FCSTD DOCUMENT  (FreeCAD 0.21R33771 (Git))
Label: RING0
License: All rights reserved
LicenseURL: http://en.wikipedia.org/wiki/All_rights_reserved
objects: Part::Part2DObjectPython×168, App::FeaturePython×24, App::DocumentObjectGroup×2
note: 168 computed .brp shape members not serialized (recipe doc carries the construction recipe); baked Part::Feature solids carry a one-line shape summary decoded from their .brp

FEATURE [Part::Part2DObjectPython] Rectangle  # Draft 2D object (typed FeaturePython)
  Area = 0
  ChamferSize = 0
  Columns = 1
  FilletRadius = 0
  Height = 6
  Length = 6
  MakeFace = false
  Placement = pos=(275.649,-48.4904,0) rot=(0,0,1;1.77186rad)
  Rows = 1
FEATURE [App::FeaturePython] Text  # WARN: FeaturePython — macro-defined, semantics opaque (R4)
  Placement = pos=(270.79,-53.3517,0) rot=(0,0,-1;4.73892rad)
  Text = 0
FEATURE [App::FeaturePython] Text001  # WARN: FeaturePython — macro-defined, semantics opaque (R4)
  Placement = pos=(268.047,49.5386,0) rot=(0,0,1;2.6241rad)
  Text = 6.
FEATURE [Part::Part2DObjectPython] Circle  # Draft 2D object (typed FeaturePython)
  Area = 1.13097
  FirstAngle = 0
  LastAngle = 0
  MakeFace = true
  Placement = pos=(271.391,-42.6225,0) rot=(0,0,1;1.77186rad)
  Radius = 0.6
FEATURE [Part::Part2DObjectPython] Rectangle001  # Draft 2D object (typed FeaturePython)
  Area = 0
  ChamferSize = 0
  Columns = 1
  FilletRadius = 0
  Height = 6
  Length = 6
  MakeFace = false
  Placement = pos=(277.924,-33.0065,0) rot=(0,0,1;1.823rad)
  Rows = 1
FEATURE [Part::Part2DObjectPython] Circle001  # Draft 2D object (typed FeaturePython)
  Area = 1.13097
  FirstAngle = 0
  LastAngle = 0
  MakeFace = true
  Placement = pos=(273.372,-27.3639,0) rot=(0,0,1;1.823rad)
  Radius = 0.6
FEATURE [Part::Part2DObjectPython] Rectangle002  # Draft 2D object (typed FeaturePython)
  Area = 0
  ChamferSize = 0
  Columns = 1
  FilletRadius = 0
  Height = 6
  Length = 6
  MakeFace = false
  Placement = pos=(279.312,-17.449,0) rot=(0,0,1;1.86558rad)
  Rows = 1
FEATURE [Part::Part2DObjectPython] Circle002  # Draft 2D object (typed FeaturePython)
  Area = 1.13097
  FirstAngle = 0
  LastAngle = 0
  MakeFace = true
  Placement = pos=(274.524,-12.0053,0) rot=(0,0,1;1.86558rad)
  Radius = 0.6
FEATURE [Part::Part2DObjectPython] Rectangle003  # Draft 2D object (typed FeaturePython)
  Area = 0
  ChamferSize = 0
  Columns = 1
  FilletRadius = 0
  Height = 6
  Length = 6
  MakeFace = false
  Placement = pos=(279.797,-1.89239,0) rot=(0,0,1;1.89386rad)
  Rows = 1
FEATURE [Part::Part2DObjectPython] Circle003  # Draft 2D object (typed FeaturePython)
  Area = 1.13097
  FirstAngle = 0
  LastAngle = 0
  MakeFace = true
  Placement = pos=(274.857,3.41377,0) rot=(0,0,1;1.89386rad)
  Radius = 0.6
FEATURE [Part::Part2DObjectPython] Rectangle004  # Draft 2D object (typed FeaturePython)
  Area = 0
  ChamferSize = 0
  Columns = 1
  FilletRadius = 0
  Height = 6
  Length = 6
  MakeFace = false
  Placement = pos=(279.385,13.5935,0) rot=(0,0,1;1.90328rad)
  Rows = 1
FEATURE [Part::Part2DObjectPython] Circle004  # Draft 2D object (typed FeaturePython)
  Area = 1.13097
  FirstAngle = 0
  LastAngle = 0
  MakeFace = true
  Placement = pos=(274.395,18.8528,0) rot=(0,0,1;1.90328rad)
  Radius = 0.6
FEATURE [Part::Part2DObjectPython] Rectangle005  # Draft 2D object (typed FeaturePython)
  Area = 0
  ChamferSize = 0
  Columns = 1
  FilletRadius = 0
  Height = 6
  Length = 6
  MakeFace = false
  Placement = pos=(278.071,28.9642,0) rot=(0,0,1;1.8956rad)
  Rows = 1
FEATURE [Part::Part2DObjectPython] Circle005  # Draft 2D object (typed FeaturePython)
  Area = 1.13097
  FirstAngle = 0
  LastAngle = 0
  MakeFace = true
  Placement = pos=(273.121,34.2618,0) rot=(0,0,1;1.8956rad)
  Radius = 0.6
FEATURE [Part::Part2DObjectPython] Rectangle006  # Draft 2D object (typed FeaturePython)
  Area = 0
  ChamferSize = 0
  Columns = 1
  FilletRadius = 0
  Height = 6
  Length = 6
  MakeFace = false
  Placement = pos=(275.882,44.2081,0) rot=(0,0,1;1.88077rad)
  Rows = 1
FEATURE [Part::Part2DObjectPython] Circle006  # Draft 2D object (typed FeaturePython)
  Area = 1.13097
  FirstAngle = 0
  LastAngle = 0
  MakeFace = true
  Placement = pos=(271.012,49.5784,0) rot=(0,0,1;1.88077rad)
  Radius = 0.6
FEATURE [Part::Part2DObjectPython] Rectangle007  # Draft 2D object (typed FeaturePython)
  Area = 0
  ChamferSize = 0
  Columns = 1
  FilletRadius = 0
  Height = 6
  Length = 6
  MakeFace = false
  Placement = pos=(262.844,95.0543,0) rot=(0,0,1;2.10958rad)
  Rows = 1
FEATURE [App::FeaturePython] Text002  # WARN: FeaturePython — macro-defined, semantics opaque (R4)
  Placement = pos=(261.188,89.1931,0) rot=(0,0,-1;4.21532rad)
  Text = 0
FEATURE [App::FeaturePython] Text003  # WARN: FeaturePython — macro-defined, semantics opaque (R4)
  Placement = pos=(207.363,176.926,0) rot=(0,0,1;3.1477rad)
  Text = 7
FEATURE [Part::Part2DObjectPython] Circle007  # Draft 2D object (typed FeaturePython)
  Area = 1.13097
  FirstAngle = 0
  LastAngle = 0
  MakeFace = true
  Placement = pos=(256.883,99.18,0) rot=(0,0,1;2.10958rad)
  Radius = 0.6
FEATURE [Part::Part2DObjectPython] Rectangle008  # Draft 2D object (typed FeaturePython)
  Area = 0
  ChamferSize = 0
  Columns = 1
  FilletRadius = 0
  Height = 6
  Length = 6
  MakeFace = false
  Placement = pos=(257.154,110.988,0) rot=(0,0,1;2.49058rad)
  Rows = 1
FEATURE [Part::Part2DObjectPython] Circle008  # Draft 2D object (typed FeaturePython)
  Area = 1.13097
  FirstAngle = 0
  LastAngle = 0
  MakeFace = true
  Placement = pos=(250.086,112.602,0) rot=(0,0,1;2.49058rad)
  Radius = 0.6
FEATURE [Part::Part2DObjectPython] Rectangle009  # Draft 2D object (typed FeaturePython)
  Area = 0
  ChamferSize = 0
  Columns = 1
  FilletRadius = 0
  Height = 6
  Length = 6
  MakeFace = false
  Placement = pos=(247.728,128.429,0) rot=(0,0,1;3.60114rad)
  Rows = 1
FEATURE [Part::Part2DObjectPython] Circle009  # Draft 2D object (typed FeaturePython)
  Area = 1.13097
  FirstAngle = 0
  LastAngle = 0
  MakeFace = true
  Placement = pos=(243.143,122.813,0) rot=(0,0,1;3.60114rad)
  Radius = 0.6
FEATURE [Part::Part2DObjectPython] Rectangle010  # Draft 2D object (typed FeaturePython)
  Area = 0
  ChamferSize = 0
  Columns = 1
  FilletRadius = 0
  Height = 6
  Length = 6
  MakeFace = false
  Placement = pos=(236.735,141.575,0) rot=(0,0,1;4.49579rad)
  Rows = 1
FEATURE [Part::Part2DObjectPython] Circle010  # Draft 2D object (typed FeaturePython)
  Area = 1.13097
  FirstAngle = 0
  LastAngle = 0
  MakeFace = true
  Placement = pos=(238.246,134.484,0) rot=(0,0,1;4.49579rad)
  Radius = 0.6
FEATURE [Part::Part2DObjectPython] Rectangle011  # Draft 2D object (typed FeaturePython)
  Area = 0
  ChamferSize = 0
  Columns = 1
  FilletRadius = 0
  Height = 6
  Length = 6
  MakeFace = false
  Placement = pos=(227.423,153.562,0) rot=(0,0,1;4.896rad)
  Rows = 1
FEATURE [Part::Part2DObjectPython] Circle011  # Draft 2D object (typed FeaturePython)
  Area = 1.13097
  FirstAngle = 0
  LastAngle = 0
  MakeFace = true
  Placement = pos=(231.577,147.621,0) rot=(0,0,1;4.896rad)
  Radius = 0.6
FEATURE [Part::Part2DObjectPython] Rectangle012  # Draft 2D object (typed FeaturePython)
  Area = 0
  ChamferSize = 0
  Columns = 1
  FilletRadius = 0
  Height = 6
  Length = 6
  MakeFace = false
  Placement = pos=(218.11,165.292,0) rot=(0,0,1;5.15099rad)
  Rows = 1
FEATURE [Part::Part2DObjectPython] Circle012  # Draft 2D object (typed FeaturePython)
  Area = 1.13097
  FirstAngle = 0
  LastAngle = 0
  MakeFace = true
  Placement = pos=(223.629,160.591,0) rot=(0,0,1;5.15099rad)
  Radius = 0.6
FEATURE [Part::Part2DObjectPython] Rectangle013  # Draft 2D object (typed FeaturePython)
  Area = 0
  ChamferSize = 0
  Columns = 1
  FilletRadius = 0
  Height = 6
  Length = 6
  MakeFace = false
  Placement = pos=(208.376,176.591,0) rot=(0,0,1;5.36287rad)
  Rows = 1
FEATURE [Part::Part2DObjectPython] Circle013  # Draft 2D object (typed FeaturePython)
  Area = 1.13097
  FirstAngle = 0
  LastAngle = 0
  MakeFace = true
  Placement = pos=(214.76,173.155,0) rot=(0,0,1;5.36287rad)
  Radius = 0.6
FEATURE [Part::Part2DObjectPython] Rectangle014  # Draft 2D object (typed FeaturePython)
  Area = 0
  ChamferSize = 0
  Columns = 1
  FilletRadius = 0
  Height = 6
  Length = 6
  MakeFace = false
  Placement = pos=(172.246,210.641,0) rot=(0,0,1;5.97234rad)
  Rows = 1
FEATURE [App::FeaturePython] Text004  # WARN: FeaturePython — macro-defined, semantics opaque (R4)
  Placement = pos=(181.597,207.836,0) rot=(0,0,-1;3.69172rad)
  Text = 0
FEATURE [App::FeaturePython] Text005  # WARN: FeaturePython — macro-defined, semantics opaque (R4)
  Placement = pos=(91.1209,256.902,0) rot=(0,0,1;3.6713rad)
  Text = 8
FEATURE [Part::Part2DObjectPython] Circle014  # Draft 2D object (typed FeaturePython)
  Area = 1.13097
  FirstAngle = 0
  LastAngle = 0
  MakeFace = true
  Placement = pos=(179.447,211.479,0) rot=(0,0,1;5.97234rad)
  Radius = 0.6
FEATURE [Part::Part2DObjectPython] Rectangle015  # Draft 2D object (typed FeaturePython)
  Area = 0
  ChamferSize = 0
  Columns = 1
  FilletRadius = 0
  Height = 6
  Length = 6
  MakeFace = false
  Placement = pos=(160.438,219.579,0) rot=(0,0,1;6.13413rad)
  Rows = 1
FEATURE [Part::Part2DObjectPython] Circle015  # Draft 2D object (typed FeaturePython)
  Area = 1.13097
  FirstAngle = 0
  LastAngle = 0
  MakeFace = true
  Placement = pos=(167.41,221.565,0) rot=(0,0,1;6.13413rad)
  Radius = 0.6
FEATURE [Part::Part2DObjectPython] Rectangle016  # Draft 2D object (typed FeaturePython)
  Area = 0
  ChamferSize = 0
  Columns = 1
  FilletRadius = 0
  Height = 6
  Length = 6
  MakeFace = false
  Placement = pos=(148.157,227.923,0) rot=(0,0,1;6.28214rad)
  Rows = 1
FEATURE [Part::Part2DObjectPython] Circle016  # Draft 2D object (typed FeaturePython)
  Area = 1.13097
  FirstAngle = 0
  LastAngle = 0
  MakeFace = true
  Placement = pos=(154.76,230.916,0) rot=(0,0,1;6.28214rad)
  Radius = 0.6
FEATURE [Part::Part2DObjectPython] Rectangle017  # Draft 2D object (typed FeaturePython)
  Area = 0
  ChamferSize = 0
  Columns = 1
  FilletRadius = 0
  Height = 6
  Length = 6
  MakeFace = false
  Placement = pos=(135.397,235.67,0) rot=(0,0,1;0.124791rad)
  Rows = 1
FEATURE [Part::Part2DObjectPython] Circle017  # Draft 2D object (typed FeaturePython)
  Area = 1.13097
  FirstAngle = 0
  LastAngle = 0
  MakeFace = true
  Placement = pos=(141.572,239.468,0) rot=(0,0,1;0.124791rad)
  Radius = 0.6
FEATURE [Part::Part2DObjectPython] Rectangle018  # Draft 2D object (typed FeaturePython)
  Area = 0
  ChamferSize = 0
  Columns = 1
  FilletRadius = 0
  Height = 6
  Length = 6
  MakeFace = false
  Placement = pos=(122.129,242.793,0) rot=(0,0,1;0.217817rad)
  Rows = 1
FEATURE [Part::Part2DObjectPython] Circle018  # Draft 2D object (typed FeaturePython)
  Area = 1.13097
  FirstAngle = 0
  LastAngle = 0
  MakeFace = true
  Placement = pos=(127.925,247.148,0) rot=(0,0,1;0.217817rad)
  Radius = 0.6
FEATURE [Part::Part2DObjectPython] Rectangle019  # Draft 2D object (typed FeaturePython)
  Area = 0
  ChamferSize = 0
  Columns = 1
  FilletRadius = 0
  Height = 6
  Length = 6
  MakeFace = false
  Placement = pos=(108.265,249.296,0) rot=(0,0,1;0.252549rad)
  Rows = 1
FEATURE [Part::Part2DObjectPython] Circle019  # Draft 2D object (typed FeaturePython)
  Area = 1.13097
  FirstAngle = 0
  LastAngle = 0
  MakeFace = true
  Placement = pos=(113.906,253.85,0) rot=(0,0,1;0.252549rad)
  Radius = 0.6
FEATURE [Part::Part2DObjectPython] Rectangle020  # Draft 2D object (typed FeaturePython)
  Area = 0
  ChamferSize = 0
  Columns = 1
  FilletRadius = 0
  Height = 6
  Length = 6
  MakeFace = false
  Placement = pos=(93.6729,255.243,0) rot=(0,0,1;0.179245rad)
  Rows = 1
FEATURE [Part::Part2DObjectPython] Circle020  # Draft 2D object (typed FeaturePython)
  Area = 1.13097
  FirstAngle = 0
  LastAngle = 0
  MakeFace = true
  Placement = pos=(99.6323,259.372,0) rot=(0,0,1;0.179245rad)
  Radius = 0.6
FEATURE [Part::Part2DObjectPython] Rectangle021  # Draft 2D object (typed FeaturePython)
  Area = 0
  ChamferSize = 0
  Columns = 1
  FilletRadius = 0
  Height = 6
  Length = 6
  MakeFace = false
  Placement = pos=(42.0451,271.038,0) rot=(0,0,1;5.7533rad)
  Rows = 1
FEATURE [App::FeaturePython] Text006  # WARN: FeaturePython — macro-defined, semantics opaque (R4)
  Placement = pos=(53.3517,270.79,0) rot=(0,0,-1;3.16812rad)
  Text = 0
FEATURE [App::FeaturePython] Text007  # WARN: FeaturePython — macro-defined, semantics opaque (R4)
  Placement = pos=(-49.5386,268.047,0) rot=(0,0,1;4.1949rad)
  Text = 9
FEATURE [Part::Part2DObjectPython] Circle021  # Draft 2D object (typed FeaturePython)
  Area = 1.13097
  FirstAngle = 0
  LastAngle = 0
  MakeFace = true
  Placement = pos=(49.2563,270.29,0) rot=(0,0,1;5.7533rad)
  Radius = 0.6
FEATURE [Part::Part2DObjectPython] Rectangle022  # Draft 2D object (typed FeaturePython)
  Area = 0
  ChamferSize = 0
  Columns = 1
  FilletRadius = 0
  Height = 6
  Length = 6
  MakeFace = false
  Placement = pos=(27.2061,272.097,0) rot=(0,0,1;6.03552rad)
  Rows = 1
FEATURE [Part::Part2DObjectPython] Circle022  # Draft 2D object (typed FeaturePython)
  Area = 1.13097
  FirstAngle = 0
  LastAngle = 0
  MakeFace = true
  Placement = pos=(34.3402,273.388,0) rot=(0,0,1;6.03552rad)
  Radius = 0.6
FEATURE [Part::Part2DObjectPython] Rectangle023  # Draft 2D object (typed FeaturePython)
  Area = 0
  ChamferSize = 0
  Columns = 1
  FilletRadius = 0
  Height = 6
  Length = 6
  MakeFace = false
  Placement = pos=(17.0338,271.634,0) rot=(0,0,1;1.16797rad)
  Rows = 1
FEATURE [Part::Part2DObjectPython] Circle023  # Draft 2D object (typed FeaturePython)
  Area = 1.13097
  FirstAngle = 0
  LastAngle = 0
  MakeFace = true
  Placement = pos=(16.8613,278.882,0) rot=(0,0,1;1.16797rad)
  Radius = 0.6
FEATURE [Part::Part2DObjectPython] Rectangle024  # Draft 2D object (typed FeaturePython)
  Area = 0
  ChamferSize = 0
  Columns = 1
  FilletRadius = 0
  Height = 6
  Length = 6
  MakeFace = false
  Placement = pos=(3.71464,273.95,0) rot=(0,0,1;1.85197rad)
  Rows = 1
FEATURE [Part::Part2DObjectPython] Circle024  # Draft 2D object (typed FeaturePython)
  Area = 1.13097
  FirstAngle = 0
  LastAngle = 0
  MakeFace = true
  Placement = pos=(-0.998936,279.459,0) rot=(0,0,1;1.85197rad)
  Radius = 0.6
FEATURE [Part::Part2DObjectPython] Rectangle025  # Draft 2D object (typed FeaturePython)
  Area = 0
  ChamferSize = 0
  Columns = 1
  FilletRadius = 0
  Height = 6
  Length = 6
  MakeFace = false
  Placement = pos=(-11.3587,274.447,0) rot=(0,0,1;2.08829rad)
  Rows = 1
FEATURE [Part::Part2DObjectPython] Circle025  # Draft 2D object (typed FeaturePython)
  Area = 1.13097
  FirstAngle = 0
  LastAngle = 0
  MakeFace = true
  Placement = pos=(-17.2309,278.699,0) rot=(0,0,1;2.08829rad)
  Radius = 0.6
FEATURE [Part::Part2DObjectPython] Rectangle026  # Draft 2D object (typed FeaturePython)
  Area = 0
  ChamferSize = 0
  Columns = 1
  FilletRadius = 0
  Height = 6
  Length = 6
  MakeFace = false
  Placement = pos=(-26.6422,273.727,0) rot=(0,0,1;2.22791rad)
  Rows = 1
FEATURE [Part::Part2DObjectPython] Circle026  # Draft 2D object (typed FeaturePython)
  Area = 1.13097
  FirstAngle = 0
  LastAngle = 0
  MakeFace = true
  Placement = pos=(-33.049,277.12,0) rot=(0,0,1;2.22791rad)
  Radius = 0.6
FEATURE [Part::Part2DObjectPython] Rectangle027  # Draft 2D object (typed FeaturePython)
  Area = 0
  ChamferSize = 0
  Columns = 1
  FilletRadius = 0
  Height = 6
  Length = 6
  MakeFace = false
  Placement = pos=(-41.9084,272.015,0) rot=(0,0,1;2.33385rad)
  Rows = 1
FEATURE [Part::Part2DObjectPython] Circle027  # Draft 2D object (typed FeaturePython)
  Area = 1.13097
  FirstAngle = 0
  LastAngle = 0
  MakeFace = true
  Placement = pos=(-48.6381,274.712,0) rot=(0,0,1;2.33385rad)
  Radius = 0.6
FEATURE [Part::Part2DObjectPython] Rectangle028  # Draft 2D object (typed FeaturePython)
  Area = 0
  ChamferSize = 0
  Columns = 1
  FilletRadius = 0
  Height = 6
  Length = 6
  MakeFace = false
  Placement = pos=(-92.004,259.872,0) rot=(0,0,1;2.62881rad)
  Rows = 1
FEATURE [App::FeaturePython] Text008  # WARN: FeaturePython — macro-defined, semantics opaque (R4)
  Placement = pos=(-89.1931,261.188,0) rot=(0,0,-1;2.64452rad)
  Text = 0
FEATURE [App::FeaturePython] Text009  # WARN: FeaturePython — macro-defined, semantics opaque (R4)
  Placement = pos=(-176.926,207.363,0) rot=(0,0,1;4.7185rad)
  Text = 10
FEATURE [Part::Part2DObjectPython] Circle028  # Draft 2D object (typed FeaturePython)
  Area = 1.13097
  FirstAngle = 0
  LastAngle = 0
  MakeFace = true
  Placement = pos=(-99.227,260.496,0) rot=(0,0,1;2.62881rad)
  Radius = 0.6
FEATURE [Part::Part2DObjectPython] Rectangle029  # Draft 2D object (typed FeaturePython)
  Area = 0
  ChamferSize = 0
  Columns = 1
  FilletRadius = 0
  Height = 6
  Length = 6
  MakeFace = false
  Placement = pos=(-106.463,254.481,0) rot=(0,0,1;2.72551rad)
  Rows = 1
FEATURE [Part::Part2DObjectPython] Circle029  # Draft 2D object (typed FeaturePython)
  Area = 1.13097
  FirstAngle = 0
  LastAngle = 0
  MakeFace = true
  Placement = pos=(-113.713,254.405,0) rot=(0,0,1;2.72551rad)
  Radius = 0.6
FEATURE [Part::Part2DObjectPython] Rectangle030  # Draft 2D object (typed FeaturePython)
  Area = 0
  ChamferSize = 0
  Columns = 1
  FilletRadius = 0
  Height = 6
  Length = 6
  MakeFace = false
  Placement = pos=(-120.643,248.321,0) rot=(0,0,1;2.83407rad)
  Rows = 1
FEATURE [Part::Part2DObjectPython] Circle030  # Draft 2D object (typed FeaturePython)
  Area = 1.13097
  FirstAngle = 0
  LastAngle = 0
  MakeFace = true
  Placement = pos=(-127.841,247.46,0) rot=(0,0,1;2.83407rad)
  Radius = 0.6
FEATURE [Part::Part2DObjectPython] Rectangle031  # Draft 2D object (typed FeaturePython)
  Area = 0
  ChamferSize = 0
  Columns = 1
  FilletRadius = 0
  Height = 6
  Length = 6
  MakeFace = false
  Placement = pos=(-135.001,242.021,0) rot=(0,0,1;3.14194rad)
  Rows = 1
FEATURE [Part::Part2DObjectPython] Circle031  # Draft 2D object (typed FeaturePython)
  Area = 1.13097
  FirstAngle = 0
  LastAngle = 0
  MakeFace = true
  Placement = pos=(-141.6,239.019,0) rot=(0,0,1;3.14194rad)
  Radius = 0.6
FEATURE [Part::Part2DObjectPython] Rectangle032  # Draft 2D object (typed FeaturePython)
  Area = 0
  ChamferSize = 0
  Columns = 1
  FilletRadius = 0
  Height = 6
  Length = 6
  MakeFace = false
  Placement = pos=(-148.162,233.922,0) rot=(0,0,1;3.14229rad)
  Rows = 1
FEATURE [Part::Part2DObjectPython] Circle032  # Draft 2D object (typed FeaturePython)
  Area = 1.13097
  FirstAngle = 0
  LastAngle = 0
  MakeFace = true
  Placement = pos=(-154.76,230.917,0) rot=(0,0,1;3.14229rad)
  Radius = 0.6
FEATURE [Part::Part2DObjectPython] Rectangle033  # Draft 2D object (typed FeaturePython)
  Area = 0
  ChamferSize = 0
  Columns = 1
  FilletRadius = 0
  Height = 6
  Length = 6
  MakeFace = false
  Placement = pos=(-161.278,225.474,0) rot=(0,0,1;3.27563rad)
  Rows = 1
FEATURE [Part::Part2DObjectPython] Circle033  # Draft 2D object (typed FeaturePython)
  Area = 1.13097
  FirstAngle = 0
  LastAngle = 0
  MakeFace = true
  Placement = pos=(-167.418,221.619,0) rot=(0,0,1;3.27563rad)
  Radius = 0.6
FEATURE [Part::Part2DObjectPython] Rectangle034  # Draft 2D object (typed FeaturePython)
  Area = 0
  ChamferSize = 0
  Columns = 1
  FilletRadius = 0
  Height = 6
  Length = 6
  MakeFace = false
  Placement = pos=(-174.05,216.338,0) rot=(0,0,1;3.44423rad)
  Rows = 1
FEATURE [Part::Part2DObjectPython] Circle034  # Draft 2D object (typed FeaturePython)
  Area = 1.13097
  FirstAngle = 0
  LastAngle = 0
  MakeFace = true
  Placement = pos=(-179.456,211.507,0) rot=(0,0,1;3.44423rad)
  Radius = 0.6
FEATURE [Part::Part2DObjectPython] Rectangle035  # Draft 2D object (typed FeaturePython)
  Area = 0
  ChamferSize = 0
  Columns = 1
  FilletRadius = 0
  Height = 6
  Length = 6
  MakeFace = false
  Placement = pos=(-213.973,180.027,0) rot=(0,0,1;4.26157rad)
  Rows = 1
FEATURE [App::FeaturePython] Text010  # WARN: FeaturePython — macro-defined, semantics opaque (R4)
  Placement = pos=(-207.836,181.597,0) rot=(0,0,-1;2.12092rad)
  Text = 0
FEATURE [App::FeaturePython] Text011  # WARN: FeaturePython — macro-defined, semantics opaque (R4)
  Placement = pos=(-256.902,91.1209,0) rot=(0,0,1;5.2421rad)
  Text = 11
FEATURE [Part::Part2DObjectPython] Circle035  # Draft 2D object (typed FeaturePython)
  Area = 1.13097
  FirstAngle = 0
  LastAngle = 0
  MakeFace = true
  Placement = pos=(-214.149,172.78,0) rot=(0,0,1;4.26157rad)
  Radius = 0.6
FEATURE [Part::Part2DObjectPython] Rectangle036  # Draft 2D object (typed FeaturePython)
  Area = 0
  ChamferSize = 0
  Columns = 1
  FilletRadius = 0
  Height = 6
  Length = 6
  MakeFace = false
  Placement = pos=(-224.768,167.149,0) rot=(0,0,1;4.60715rad)
  Rows = 1
FEATURE [Part::Part2DObjectPython] Circle036  # Draft 2D object (typed FeaturePython)
  Area = 1.13097
  FirstAngle = 0
  LastAngle = 0
  MakeFace = true
  Placement = pos=(-222.478,160.27,0) rot=(0,0,1;4.60715rad)
  Radius = 0.6
FEATURE [Part::Part2DObjectPython] Rectangle037  # Draft 2D object (typed FeaturePython)
  Area = 0
  ChamferSize = 0
  Columns = 1
  FilletRadius = 0
  Height = 6
  Length = 6
  MakeFace = false
  Placement = pos=(-234.676,153.133,0) rot=(0,0,1;5.01416rad)
  Rows = 1
FEATURE [Part::Part2DObjectPython] Circle037  # Draft 2D object (typed FeaturePython)
  Area = 1.13097
  FirstAngle = 0
  LastAngle = 0
  MakeFace = true
  Placement = pos=(-229.85,147.723,0) rot=(0,0,1;5.01416rad)
  Radius = 0.6
FEATURE [Part::Part2DObjectPython] Rectangle038  # Draft 2D object (typed FeaturePython)
  Area = 0
  ChamferSize = 0
  Columns = 1
  FilletRadius = 0
  Height = 6
  Length = 6
  MakeFace = false
  Placement = pos=(-243.261,138.127,0) rot=(0,0,1;5.46794rad)
  Rows = 1
FEATURE [Part::Part2DObjectPython] Circle038  # Draft 2D object (typed FeaturePython)
  Area = 1.13097
  FirstAngle = 0
  LastAngle = 0
  MakeFace = true
  Placement = pos=(-236.552,135.38,0) rot=(0,0,1;5.46794rad)
  Radius = 0.6
FEATURE [Part::Part2DObjectPython] Rectangle039  # Draft 2D object (typed FeaturePython)
  Area = 0
  ChamferSize = 0
  Columns = 1
  FilletRadius = 0
  Height = 6
  Length = 6
  MakeFace = false
  Placement = pos=(-250.243,122.679,0) rot=(0,0,1;5.91806rad)
  Rows = 1
FEATURE [Part::Part2DObjectPython] Circle039  # Draft 2D object (typed FeaturePython)
  Area = 1.13097
  FirstAngle = 0
  LastAngle = 0
  MakeFace = true
  Placement = pos=(-243.007,123.125,0) rot=(0,0,1;5.91806rad)
  Radius = 0.6
FEATURE [Part::Part2DObjectPython] Rectangle040  # Draft 2D object (typed FeaturePython)
  Area = 0
  ChamferSize = 0
  Columns = 1
  FilletRadius = 0
  Height = 6
  Length = 6
  MakeFace = false
  Placement = pos=(-255.827,107.302,0) rot=(0,0,1;0.040317rad)
  Rows = 1
FEATURE [Part::Part2DObjectPython] Circle040  # Draft 2D object (typed FeaturePython)
  Area = 1.13097
  FirstAngle = 0
  LastAngle = 0
  MakeFace = true
  Placement = pos=(-249.353,110.565,0) rot=(0,0,1;0.040317rad)
  Radius = 0.6
FEATURE [Part::Part2DObjectPython] Rectangle041  # Draft 2D object (typed FeaturePython)
  Area = 0
  ChamferSize = 0
  Columns = 1
  FilletRadius = 0
  Height = 6
  Length = 6
  MakeFace = false
  Placement = pos=(-260.388,92.1849,0) rot=(0,0,1;0.383798rad)
  Rows = 1
FEATURE [Part::Part2DObjectPython] Circle041  # Draft 2D object (typed FeaturePython)
  Area = 1.13097
  FirstAngle = 0
  LastAngle = 0
  MakeFace = true
  Placement = pos=(-255.392,97.438,0) rot=(0,0,1;0.383798rad)
  Radius = 0.6
FEATURE [Part::Part2DObjectPython] Rectangle042  # Draft 2D object (typed FeaturePython)
  Area = 0
  ChamferSize = 0
  Columns = 1
  FilletRadius = 0
  Height = 6
  Length = 6
  MakeFace = false
  Placement = pos=(-270.401,42.267,0) rot=(0,0,1;1.20009rad)
  Rows = 1
FEATURE [App::FeaturePython] Text012  # WARN: FeaturePython — macro-defined, semantics opaque (R4)
  Placement = pos=(-270.79,53.3517,0) rot=(0,0,-1;1.59733rad)
  Text = 0
FEATURE [App::FeaturePython] Text013  # WARN: FeaturePython — macro-defined, semantics opaque (R4)
  Placement = pos=(-268.047,-49.5386,0) rot=(0,0,1;5.7657rad)
  Text = 12
FEATURE [Part::Part2DObjectPython] Circle042  # Draft 2D object (typed FeaturePython)
  Area = 1.13097
  FirstAngle = 0
  LastAngle = 0
  MakeFace = true
  Placement = pos=(-270.806,49.5055,0) rot=(0,0,1;1.20009rad)
  Radius = 0.6
FEATURE [Part::Part2DObjectPython] Rectangle043  # Draft 2D object (typed FeaturePython)
  Area = 0
  ChamferSize = 0
  Columns = 1
  FilletRadius = 0
  Height = 6
  Length = 6
  MakeFace = false
  Placement = pos=(-271.894,27.3348,0) rot=(0,0,1;1.37968rad)
  Rows = 1
FEATURE [Part::Part2DObjectPython] Circle043  # Draft 2D object (typed FeaturePython)
  Area = 1.13097
  FirstAngle = 0
  LastAngle = 0
  MakeFace = true
  Placement = pos=(-273.586,34.3845,0) rot=(0,0,1;1.37968rad)
  Radius = 0.6
FEATURE [Part::Part2DObjectPython] Rectangle044  # Draft 2D object (typed FeaturePython)
  Area = 0
  ChamferSize = 0
  Columns = 1
  FilletRadius = 0
  Height = 6
  Length = 6
  MakeFace = false
  Placement = pos=(-272.673,12.3507,0) rot=(0,0,1;1.53711rad)
  Rows = 1
FEATURE [Part::Part2DObjectPython] Circle044  # Draft 2D object (typed FeaturePython)
  Area = 1.13097
  FirstAngle = 0
  LastAngle = 0
  MakeFace = true
  Placement = pos=(-275.449,19.048,0) rot=(0,0,1;1.53711rad)
  Radius = 0.6
FEATURE [Part::Part2DObjectPython] Rectangle045  # Draft 2D object (typed FeaturePython)
  Area = 0
  ChamferSize = 0
  Columns = 1
  FilletRadius = 0
  Height = 6
  Length = 6
  MakeFace = false
  Placement = pos=(-272.708,-2.67631,0) rot=(0,0,1;1.6736rad)
  Rows = 1
FEATURE [Part::Part2DObjectPython] Circle045  # Draft 2D object (typed FeaturePython)
  Area = 1.13097
  FirstAngle = 0
  LastAngle = 0
  MakeFace = true
  Placement = pos=(-276.369,3.58099,0) rot=(0,0,1;1.6736rad)
  Radius = 0.6
FEATURE [Part::Part2DObjectPython] Rectangle046  # Draft 2D object (typed FeaturePython)
  Area = 0
  ChamferSize = 0
  Columns = 1
  FilletRadius = 0
  Height = 6
  Length = 6
  MakeFace = false
  Placement = pos=(-271.992,-17.7302,0) rot=(0,0,1;1.78879rad)
  Rows = 1
FEATURE [Part::Part2DObjectPython] Circle046  # Draft 2D object (typed FeaturePython)
  Area = 1.13097
  FirstAngle = 0
  LastAngle = 0
  MakeFace = true
  Placement = pos=(-276.349,-11.9352,0) rot=(0,0,1;1.78879rad)
  Radius = 0.6
FEATURE [Part::Part2DObjectPython] Rectangle047  # Draft 2D object (typed FeaturePython)
  Area = 0
  ChamferSize = 0
  Columns = 1
  FilletRadius = 0
  Height = 6
  Length = 6
  MakeFace = false
  Placement = pos=(-270.491,-32.7781,0) rot=(0,0,1;1.88443rad)
  Rows = 1
FEATURE [Part::Part2DObjectPython] Circle047  # Draft 2D object (typed FeaturePython)
  Area = 1.13097
  FirstAngle = 0
  LastAngle = 0
  MakeFace = true
  Placement = pos=(-275.381,-27.4256,0) rot=(0,0,1;1.88443rad)
  Radius = 0.6
FEATURE [Part::Part2DObjectPython] Rectangle048  # Draft 2D object (typed FeaturePython)
  Area = 0
  ChamferSize = 0
  Columns = 1
  FilletRadius = 0
  Height = 6
  Length = 6
  MakeFace = false
  Placement = pos=(-268.197,-47.7893,0) rot=(0,0,1;1.95948rad)
  Rows = 1
FEATURE [Part::Part2DObjectPython] Circle048  # Draft 2D object (typed FeaturePython)
  Area = 1.13097
  FirstAngle = 0
  LastAngle = 0
  MakeFace = true
  Placement = pos=(-273.474,-42.8185,0) rot=(0,0,1;1.95948rad)
  Radius = 0.6
FEATURE [Part::Part2DObjectPython] Rectangle049  # Draft 2D object (typed FeaturePython)
  Area = 0
  ChamferSize = 0
  Columns = 1
  FilletRadius = 0
  Height = 6
  Length = 6
  MakeFace = false
  Placement = pos=(-254.618,-97.1336,0) rot=(0,0,1;2.10766rad)
  Rows = 1
FEATURE [App::FeaturePython] Text014  # WARN: FeaturePython — macro-defined, semantics opaque (R4)
  Placement = pos=(-261.188,-89.1931,0) rot=(0,0,-1;1.07373rad)
  Text = 0
FEATURE [App::FeaturePython] Text015  # WARN: FeaturePython — macro-defined, semantics opaque (R4)
  Placement = pos=(-207.363,-176.926,0) rot=(0,0,-1;6.27708rad)
  Text = 1
FEATURE [Part::Part2DObjectPython] Circle049  # Draft 2D object (typed FeaturePython)
  Area = 1.13097
  FirstAngle = 0
  LastAngle = 0
  MakeFace = true
  Placement = pos=(-260.571,-92.9965,0) rot=(0,0,1;2.10766rad)
  Radius = 0.6
FEATURE [Part::Part2DObjectPython] Rectangle050  # Draft 2D object (typed FeaturePython)
  Area = 0
  ChamferSize = 0
  Columns = 1
  FilletRadius = 0
  Height = 6
  Length = 6
  MakeFace = false
  Placement = pos=(-248.8,-111.302,0) rot=(0,0,1;2.14676rad)
  Rows = 1
FEATURE [Part::Part2DObjectPython] Circle050  # Draft 2D object (typed FeaturePython)
  Area = 1.13097
  FirstAngle = 0
  LastAngle = 0
  MakeFace = true
  Placement = pos=(-254.911,-107.401,0) rot=(0,0,1;2.14676rad)
  Radius = 0.6
FEATURE [Part::Part2DObjectPython] Rectangle051  # Draft 2D object (typed FeaturePython)
  Area = 0
  ChamferSize = 0
  Columns = 1
  FilletRadius = 0
  Height = 6
  Length = 6
  MakeFace = false
  Placement = pos=(-242.184,-125.1,0) rot=(0,0,1;2.19283rad)
  Rows = 1
FEATURE [Part::Part2DObjectPython] Circle051  # Draft 2D object (typed FeaturePython)
  Area = 1.13097
  FirstAngle = 0
  LastAngle = 0
  MakeFace = true
  Placement = pos=(-248.468,-121.484,0) rot=(0,0,1;2.19283rad)
  Radius = 0.6
FEATURE [Part::Part2DObjectPython] Rectangle052  # Draft 2D object (typed FeaturePython)
  Area = 0
  ChamferSize = 0
  Columns = 1
  FilletRadius = 0
  Height = 6
  Length = 6
  MakeFace = false
  Placement = pos=(-234.809,-138.518,0) rot=(0,0,1;2.23385rad)
  Rows = 1
FEATURE [Part::Part2DObjectPython] Circle052  # Draft 2D object (typed FeaturePython)
  Area = 1.13097
  FirstAngle = 0
  LastAngle = 0
  MakeFace = true
  Placement = pos=(-241.236,-135.163,0) rot=(0,0,1;2.23385rad)
  Radius = 0.6
FEATURE [Part::Part2DObjectPython] Rectangle053  # Draft 2D object (typed FeaturePython)
  Area = 0
  ChamferSize = 0
  Columns = 1
  FilletRadius = 0
  Height = 6
  Length = 6
  MakeFace = false
  Placement = pos=(-233.539,-154.498,0) rot=(0,0,1;0.120079rad)
  Rows = 1
FEATURE [Part::Part2DObjectPython] Circle053  # Draft 2D object (typed FeaturePython)
  Area = 1.13097
  FirstAngle = 0
  LastAngle = 0
  MakeFace = true
  Placement = pos=(-227.346,-150.729,0) rot=(0,0,1;0.120079rad)
  Radius = 0.6
FEATURE [Part::Part2DObjectPython] Rectangle054  # Draft 2D object (typed FeaturePython)
  Area = 0
  ChamferSize = 0
  Columns = 1
  FilletRadius = 0
  Height = 6
  Length = 6
  MakeFace = false
  Placement = pos=(-226.28,-164.579,0) rot=(0,0,1;5.6704rad)
  Rows = 1
FEATURE [Part::Part2DObjectPython] Circle054  # Draft 2D object (typed FeaturePython)
  Area = 1.13097
  FirstAngle = 0
  LastAngle = 0
  MakeFace = true
  Placement = pos=(-219.155,-165.921,0) rot=(0,0,1;5.6704rad)
  Radius = 0.6
FEATURE [Part::Part2DObjectPython] Rectangle055  # Draft 2D object (typed FeaturePython)
  Area = 0
  ChamferSize = 0
  Columns = 1
  FilletRadius = 0
  Height = 6
  Length = 6
  MakeFace = false
  Placement = pos=(-216.681,-177.108,0) rot=(0,0,1;5.75714rad)
  Rows = 1
FEATURE [Part::Part2DObjectPython] Circle055  # Draft 2D object (typed FeaturePython)
  Area = 1.13097
  FirstAngle = 0
  LastAngle = 0
  MakeFace = true
  Placement = pos=(-209.467,-177.828,0) rot=(0,0,1;5.75714rad)
  Radius = 0.6
FEATURE [Part::Part2DObjectPython] Rectangle056  # Draft 2D object (typed FeaturePython)
  Area = 0
  ChamferSize = 0
  Columns = 1
  FilletRadius = 0
  Height = 6
  Length = 6
  MakeFace = false
  Placement = pos=(-179.369,-215.185,0) rot=(0,0,1;6.15892rad)
  Rows = 1
FEATURE [App::FeaturePython] Text016  # WARN: FeaturePython — macro-defined, semantics opaque (R4)
  Placement = pos=(-181.597,-207.836,0) rot=(0,0,-1;0.550128rad)
  Text = 0
FEATURE [App::FeaturePython] Text017  # WARN: FeaturePython — macro-defined, semantics opaque (R4)
  Placement = pos=(-91.1209,-256.902,0) rot=(0,0,-1;5.75348rad)
  Text = 2
FEATURE [Part::Part2DObjectPython] Circle056  # Draft 2D object (typed FeaturePython)
  Area = 1.13097
  FirstAngle = 0
  LastAngle = 0
  MakeFace = true
  Placement = pos=(-172.448,-213.026,0) rot=(0,0,1;6.15892rad)
  Radius = 0.6
FEATURE [Part::Part2DObjectPython] Rectangle057  # Draft 2D object (typed FeaturePython)
  Area = 0
  ChamferSize = 0
  Columns = 1
  FilletRadius = 0
  Height = 6
  Length = 6
  MakeFace = false
  Placement = pos=(-166.838,-225.112,0) rot=(0,0,1;0.004014rad)
  Rows = 1
FEATURE [Part::Part2DObjectPython] Circle057  # Draft 2D object (typed FeaturePython)
  Area = 1.13097
  FirstAngle = 0
  LastAngle = 0
  MakeFace = true
  Placement = pos=(-160.25,-222.086,0) rot=(0,0,1;0.004014rad)
  Radius = 0.6
FEATURE [Part::Part2DObjectPython] Rectangle058  # Draft 2D object (typed FeaturePython)
  Area = 0
  ChamferSize = 0
  Columns = 1
  FilletRadius = 0
  Height = 6
  Length = 6
  MakeFace = false
  Placement = pos=(-153.734,-234.293,0) rot=(0,0,1;0.133518rad)
  Rows = 1
FEATURE [Part::Part2DObjectPython] Circle058  # Draft 2D object (typed FeaturePython)
  Area = 1.13097
  FirstAngle = 0
  LastAngle = 0
  MakeFace = true
  Placement = pos=(-147.592,-230.441,0) rot=(0,0,1;0.133518rad)
  Radius = 0.6
FEATURE [Part::Part2DObjectPython] Rectangle059  # Draft 2D object (typed FeaturePython)
  Area = 0
  ChamferSize = 0
  Columns = 1
  FilletRadius = 0
  Height = 6
  Length = 6
  MakeFace = false
  Placement = pos=(-140.112,-242.699,0) rot=(0,0,1;0.264243rad)
  Rows = 1
FEATURE [Part::Part2DObjectPython] Circle059  # Draft 2D object (typed FeaturePython)
  Area = 1.13097
  FirstAngle = 0
  LastAngle = 0
  MakeFace = true
  Placement = pos=(-134.525,-238.08,0) rot=(0,0,1;0.264243rad)
  Radius = 0.6
FEATURE [Part::Part2DObjectPython] Rectangle060  # Draft 2D object (typed FeaturePython)
  Area = 0
  ChamferSize = 0
  Columns = 1
  FilletRadius = 0
  Height = 6
  Length = 6
  MakeFace = false
  Placement = pos=(-126.019,-250.296,0) rot=(0,0,1;0.396364rad)
  Rows = 1
FEATURE [Part::Part2DObjectPython] Circle060  # Draft 2D object (typed FeaturePython)
  Area = 1.13097
  FirstAngle = 0
  LastAngle = 0
  MakeFace = true
  Placement = pos=(-121.089,-244.98,0) rot=(0,0,1;0.396364rad)
  Radius = 0.6
FEATURE [Part::Part2DObjectPython] Rectangle061  # Draft 2D object (typed FeaturePython)
  Area = 0
  ChamferSize = 0
  Columns = 1
  FilletRadius = 0
  Height = 6
  Length = 6
  MakeFace = false
  Placement = pos=(-111.489,-257.056,0) rot=(0,0,1;0.530755rad)
  Rows = 1
FEATURE [Part::Part2DObjectPython] Circle061  # Draft 2D object (typed FeaturePython)
  Area = 1.13097
  FirstAngle = 0
  LastAngle = 0
  MakeFace = true
  Placement = pos=(-107.315,-251.128,0) rot=(0,0,1;0.530755rad)
  Radius = 0.6
FEATURE [Part::Part2DObjectPython] Rectangle062  # Draft 2D object (typed FeaturePython)
  Area = 0
  ChamferSize = 0
  Columns = 1
  FilletRadius = 0
  Height = 6
  Length = 6
  MakeFace = false
  Placement = pos=(-96.5872,-262.943,0) rot=(0,0,1;0.667938rad)
  Rows = 1
FEATURE [Part::Part2DObjectPython] Circle062  # Draft 2D object (typed FeaturePython)
  Area = 1.13097
  FirstAngle = 0
  LastAngle = 0
  MakeFace = true
  Placement = pos=(-93.2636,-256.5,0) rot=(0,0,1;0.667938rad)
  Radius = 0.6
FEATURE [Part::Part2DObjectPython] Rectangle063  # Draft 2D object (typed FeaturePython)
  Area = 0
  ChamferSize = 0
  Columns = 1
  FilletRadius = 0
  Height = 6
  Length = 6
  MakeFace = false
  Placement = pos=(-44.6282,-276.07,0) rot=(0,0,1;1.15227rad)
  Rows = 1
FEATURE [App::FeaturePython] Text018  # WARN: FeaturePython — macro-defined, semantics opaque (R4)
  Placement = pos=(-53.3517,-270.79,0) rot=(0,0,1;6.25666rad)
  Text = 0
FEATURE [App::FeaturePython] Text019  # WARN: FeaturePython — macro-defined, semantics opaque (R4)
  Placement = pos=(49.5386,-268.047,0) rot=(0,0,1;1.05331rad)
  Text = 3
FEATURE [Part::Part2DObjectPython] Circle063  # Draft 2D object (typed FeaturePython)
  Area = 1.13097
  FirstAngle = 0
  LastAngle = 0
  MakeFace = true
  Placement = pos=(-44.6869,-268.821,0) rot=(0,0,1;1.15227rad)
  Radius = 0.6
FEATURE [Part::Part2DObjectPython] Rectangle064  # Draft 2D object (typed FeaturePython)
  Area = 0
  ChamferSize = 0
  Columns = 1
  FilletRadius = 0
  Height = 6
  Length = 6
  MakeFace = false
  Placement = pos=(-28.7479,-277.955,0) rot=(0,0,1;1.30376rad)
  Rows = 1
FEATURE [Part::Part2DObjectPython] Circle064  # Draft 2D object (typed FeaturePython)
  Area = 1.13097
  FirstAngle = 0
  LastAngle = 0
  MakeFace = true
  Placement = pos=(-29.9001,-270.798,0) rot=(0,0,1;1.30376rad)
  Radius = 0.6
FEATURE [Part::Part2DObjectPython] Rectangle065  # Draft 2D object (typed FeaturePython)
  Area = 0
  ChamferSize = 0
  Columns = 1
  FilletRadius = 0
  Height = 6
  Length = 6
  MakeFace = false
  Placement = pos=(-12.8077,-278.889,0) rot=(0,0,1;1.4577rad)
  Rows = 1
FEATURE [Part::Part2DObjectPython] Circle065  # Draft 2D object (typed FeaturePython)
  Area = 1.13097
  FirstAngle = 0
  LastAngle = 0
  MakeFace = true
  Placement = pos=(-15.0437,-271.993,0) rot=(0,0,1;1.4577rad)
  Radius = 0.6
FEATURE [Part::Part2DObjectPython] Rectangle066  # Draft 2D object (typed FeaturePython)
  Area = 0
  ChamferSize = 0
  Columns = 1
  FilletRadius = 0
  Height = 6
  Length = 6
  MakeFace = false
  Placement = pos=(3.1255,-278.869,0) rot=(0,0,1;1.61356rad)
  Rows = 1
FEATURE [Part::Part2DObjectPython] Circle066  # Draft 2D object (typed FeaturePython)
  Area = 1.13097
  FirstAngle = 0
  LastAngle = 0
  MakeFace = true
  Placement = pos=(-0.153891,-272.403,0) rot=(0,0,1;1.61356rad)
  Radius = 0.6
FEATURE [Part::Part2DObjectPython] Rectangle067  # Draft 2D object (typed FeaturePython)
  Area = 0
  ChamferSize = 0
  Columns = 1
  FilletRadius = 0
  Height = 6
  Length = 6
  MakeFace = false
  Placement = pos=(18.9871,-277.913,0) rot=(0,0,1;1.77116rad)
  Rows = 1
FEATURE [Part::Part2DObjectPython] Circle067  # Draft 2D object (typed FeaturePython)
  Area = 1.13097
  FirstAngle = 0
  LastAngle = 0
  MakeFace = true
  Placement = pos=(14.7335,-272.042,0) rot=(0,0,1;1.77116rad)
  Radius = 0.6
FEATURE [Part::Part2DObjectPython] Rectangle068  # Draft 2D object (typed FeaturePython)
  Area = 0
  ChamferSize = 0
  Columns = 1
  FilletRadius = 0
  Height = 6
  Length = 6
  MakeFace = false
  Placement = pos=(34.7128,-276.025,0) rot=(0,0,1;1.92981rad)
  Rows = 1
FEATURE [Part::Part2DObjectPython] Circle068  # Draft 2D object (typed FeaturePython)
  Area = 1.13097
  FirstAngle = 0
  LastAngle = 0
  MakeFace = true
  Placement = pos=(29.5851,-270.9,0) rot=(0,0,1;1.92981rad)
  Radius = 0.6
FEATURE [Part::Part2DObjectPython] Rectangle069  # Draft 2D object (typed FeaturePython)
  Area = 0
  ChamferSize = 0
  Columns = 1
  FilletRadius = 0
  Height = 6
  Length = 6
  MakeFace = false
  Placement = pos=(50.2423,-273.23,0) rot=(0,0,1;2.08916rad)
  Rows = 1
FEATURE [Part::Part2DObjectPython] Circle069  # Draft 2D object (typed FeaturePython)
  Area = 1.13097
  FirstAngle = 0
  LastAngle = 0
  MakeFace = true
  Placement = pos=(44.3663,-268.983,0) rot=(0,0,1;2.08916rad)
  Radius = 0.6
FEATURE [Part::Part2DObjectPython] Rectangle070  # Draft 2D object (typed FeaturePython)
  Area = 0
  ChamferSize = 0
  Columns = 1
  FilletRadius = 0
  Height = 6
  Length = 6
  MakeFace = false
  Placement = pos=(100.182,-257.611,0) rot=(0,0,1;2.62305rad)
  Rows = 1
FEATURE [App::FeaturePython] Text020  # WARN: FeaturePython — macro-defined, semantics opaque (R4)
  Placement = pos=(89.1931,-261.188,0) rot=(0,0,-1;5.78612rad)
  Text = 0
FEATURE [App::FeaturePython] Text021  # WARN: FeaturePython — macro-defined, semantics opaque (R4)
  Placement = pos=(176.926,-207.363,0) rot=(0,0,1;1.57691rad)
  Text = 4
FEATURE [Part::Part2DObjectPython] Circle070  # Draft 2D object (typed FeaturePython)
  Area = 1.13097
  FirstAngle = 0
  LastAngle = 0
  MakeFace = true
  Placement = pos=(92.9632,-256.946,0) rot=(0,0,1;2.62305rad)
  Radius = 0.6
FEATURE [Part::Part2DObjectPython] Rectangle071  # Draft 2D object (typed FeaturePython)
  Area = 0
  ChamferSize = 0
  Columns = 1
  FilletRadius = 0
  Height = 6
  Length = 6
  MakeFace = false
  Placement = pos=(114.286,-251.202,0) rot=(0,0,1;2.78083rad)
  Rows = 1
FEATURE [Part::Part2DObjectPython] Circle071  # Draft 2D object (typed FeaturePython)
  Area = 1.13097
  FirstAngle = 0
  LastAngle = 0
  MakeFace = true
  Placement = pos=(107.052,-251.679,0) rot=(0,0,1;2.78083rad)
  Radius = 0.6
FEATURE [Part::Part2DObjectPython] Rectangle072  # Draft 2D object (typed FeaturePython)
  Area = 0
  ChamferSize = 0
  Columns = 1
  FilletRadius = 0
  Height = 6
  Length = 6
  MakeFace = false
  Placement = pos=(127.959,-244.045,0) rot=(0,0,1;2.93617rad)
  Rows = 1
FEATURE [Part::Part2DObjectPython] Circle072  # Draft 2D object (typed FeaturePython)
  Area = 1.13097
  FirstAngle = 0
  LastAngle = 0
  MakeFace = true
  Placement = pos=(120.886,-245.636,0) rot=(0,0,1;2.93617rad)
  Radius = 0.6
FEATURE [Part::Part2DObjectPython] Rectangle073  # Draft 2D object (typed FeaturePython)
  Area = 0
  ChamferSize = 0
  Columns = 1
  FilletRadius = 0
  Height = 6
  Length = 6
  MakeFace = false
  Placement = pos=(141.187,-236.22,0) rot=(0,0,1;3.07701rad)
  Rows = 1
FEATURE [Part::Part2DObjectPython] Circle073  # Draft 2D object (typed FeaturePython)
  Area = 1.13097
  FirstAngle = 0
  LastAngle = 0
  MakeFace = true
  Placement = pos=(134.408,-238.788,0) rot=(0,0,1;3.07701rad)
  Radius = 0.6
FEATURE [Part::Part2DObjectPython] Rectangle074  # Draft 2D object (typed FeaturePython)
  Area = 0
  ChamferSize = 0
  Columns = 1
  FilletRadius = 0
  Height = 6
  Length = 6
  MakeFace = false
  Placement = pos=(154.161,-227.921,0) rot=(0,0,1;3.14124rad)
  Rows = 1
FEATURE [Part::Part2DObjectPython] Circle074  # Draft 2D object (typed FeaturePython)
  Area = 1.13097
  FirstAngle = 0
  LastAngle = 0
  MakeFace = true
  Placement = pos=(147.56,-230.919,0) rot=(0,0,1;3.14124rad)
  Radius = 0.6
FEATURE [Part::Part2DObjectPython] Rectangle075  # Draft 2D object (typed FeaturePython)
  Area = 0
  ChamferSize = 0
  Columns = 1
  FilletRadius = 0
  Height = 6
  Length = 6
  MakeFace = false
  Placement = pos=(166.85,-219.1,0) rot=(0,0,1;3.14159rad)
  Rows = 1
FEATURE [Part::Part2DObjectPython] Circle075  # Draft 2D object (typed FeaturePython)
  Area = 1.13097
  FirstAngle = 0
  LastAngle = 0
  MakeFace = true
  Placement = pos=(160.25,-222.1,0) rot=(0,0,1;3.14159rad)
  Radius = 0.6
FEATURE [Part::Part2DObjectPython] Rectangle076  # Draft 2D object (typed FeaturePython)
  Area = 0
  ChamferSize = 0
  Columns = 1
  FilletRadius = 0
  Height = 6
  Length = 6
  MakeFace = false
  Placement = pos=(179.02,-209.58,0) rot=(0,0,1;3.14159rad)
  Rows = 1
FEATURE [Part::Part2DObjectPython] Circle076  # Draft 2D object (typed FeaturePython)
  Area = 1.13097
  FirstAngle = 0
  LastAngle = 0
  MakeFace = true
  Placement = pos=(172.42,-212.58,0) rot=(0,0,1;3.14159rad)
  Radius = 0.6
FEATURE [Part::Part2DObjectPython] Rectangle077  # Draft 2D object (typed FeaturePython)
  Area = 0
  ChamferSize = 0
  Columns = 1
  FilletRadius = 0
  Height = 6
  Length = 6
  MakeFace = false
  Placement = pos=(214.572,-172.274,0) rot=(0,0,1;3.43812rad)
  Rows = 1
FEATURE [App::FeaturePython] Text022  # WARN: FeaturePython — macro-defined, semantics opaque (R4)
  Placement = pos=(207.836,-181.597,0) rot=(0,0,-1;5.26252rad)
  Text = 0
FEATURE [App::FeaturePython] Text023  # WARN: FeaturePython — macro-defined, semantics opaque (R4)
  Placement = pos=(256.902,-91.1209,0) rot=(0,0,1;2.1005rad)
  Text = 5
FEATURE [Part::Part2DObjectPython] Circle077  # Draft 2D object (typed FeaturePython)
  Area = 1.13097
  FirstAngle = 0
  LastAngle = 0
  MakeFace = true
  Placement = pos=(209.137,-177.072,0) rot=(0,0,1;3.43812rad)
  Radius = 0.6
FEATURE [Part::Part2DObjectPython] Rectangle078  # Draft 2D object (typed FeaturePython)
  Area = 0
  ChamferSize = 0
  Columns = 1
  FilletRadius = 0
  Height = 6
  Length = 6
  MakeFace = false
  Placement = pos=(225.599,-161.451,0) rot=(0,0,1;2.95711rad)
  Rows = 1
FEATURE [Part::Part2DObjectPython] Circle078  # Draft 2D object (typed FeaturePython)
  Area = 1.13097
  FirstAngle = 0
  LastAngle = 0
  MakeFace = true
  Placement = pos=(218.561,-163.19,0) rot=(0,0,1;2.95711rad)
  Radius = 0.6
FEATURE [Part::Part2DObjectPython] Rectangle079  # Draft 2D object (typed FeaturePython)
  Area = 0
  ChamferSize = 0
  Columns = 1
  FilletRadius = 0
  Height = 6
  Length = 6
  MakeFace = false
  Placement = pos=(235.153,-151.44,0) rot=(0,0,1;2.29005rad)
  Rows = 1
FEATURE [Part::Part2DObjectPython] Circle079  # Draft 2D object (typed FeaturePython)
  Area = 1.13097
  FirstAngle = 0
  LastAngle = 0
  MakeFace = true
  Placement = pos=(228.548,-148.452,0) rot=(0,0,1;2.29005rad)
  Radius = 0.6
FEATURE [Part::Part2DObjectPython] Rectangle080  # Draft 2D object (typed FeaturePython)
  Area = 0
  ChamferSize = 0
  Columns = 1
  FilletRadius = 0
  Height = 6
  Length = 6
  MakeFace = false
  Placement = pos=(242.732,-140.055,0) rot=(0,0,1;1.85057rad)
  Rows = 1
FEATURE [Part::Part2DObjectPython] Circle080  # Draft 2D object (typed FeaturePython)
  Area = 1.13097
  FirstAngle = 0
  LastAngle = 0
  MakeFace = true
  Placement = pos=(238.026,-134.54,0) rot=(0,0,1;1.85057rad)
  Radius = 0.6
FEATURE [Part::Part2DObjectPython] Rectangle081  # Draft 2D object (typed FeaturePython)
  Area = 0
  ChamferSize = 0
  Columns = 1
  FilletRadius = 0
  Height = 6
  Length = 6
  MakeFace = false
  Placement = pos=(249.678,-127.066,0) rot=(0,0,1;1.67971rad)
  Rows = 1
FEATURE [Part::Part2DObjectPython] Circle081  # Draft 2D object (typed FeaturePython)
  Area = 1.13097
  FirstAngle = 0
  LastAngle = 0
  MakeFace = true
  Placement = pos=(245.979,-120.831,0) rot=(0,0,1;1.67971rad)
  Radius = 0.6
FEATURE [Part::Part2DObjectPython] Rectangle082  # Draft 2D object (typed FeaturePython)
  Area = 0
  ChamferSize = 0
  Columns = 1
  FilletRadius = 0
  Height = 6
  Length = 6
  MakeFace = false
  Placement = pos=(256.114,-113.247,0) rot=(0,0,1;1.627rad)
  Rows = 1
FEATURE [Part::Part2DObjectPython] Circle082  # Draft 2D object (typed FeaturePython)
  Area = 1.13097
  FirstAngle = 0
  LastAngle = 0
  MakeFace = true
  Placement = pos=(252.748,-106.826,0) rot=(0,0,1;1.627rad)
  Radius = 0.6
FEATURE [Part::Part2DObjectPython] Rectangle083  # Draft 2D object (typed FeaturePython)
  Area = 0
  ChamferSize = 0
  Columns = 1
  FilletRadius = 0
  Height = 6
  Length = 6
  MakeFace = false
  Placement = pos=(261.895,-98.9151,0) rot=(0,0,1;1.62752rad)
  Rows = 1
FEATURE [Part::Part2DObjectPython] Circle083  # Draft 2D object (typed FeaturePython)
  Area = 1.13097
  FirstAngle = 0
  LastAngle = 0
  MakeFace = true
  Placement = pos=(258.526,-92.4958,0) rot=(0,0,1;1.62752rad)
  Radius = 0.6
FEATURE [App::DocumentObjectGroup] Everything
  Group = -> [Rectangle,Circle,Rectangle001,Circle001,Rectangle002,Circle002,Rectangle003,Circle003,Rectangle004,Circle004,Rectangle005,Circle005,Rectangle006,Circle006,Rectangle007,Circle007,Rectangle008,Circle008,Rectangle009,Circle009,Rectangle010,Circle010,Rectangle011,Circle011,Rectangle012,Circle012,Rectangle013,Circle013,Rectangle014,Circle014,Rectangle015,Circle015,Rectangle016,Circle016,Rectangle017,+133 more]
FEATURE [App::DocumentObjectGroup] _40726_RING0_clean
